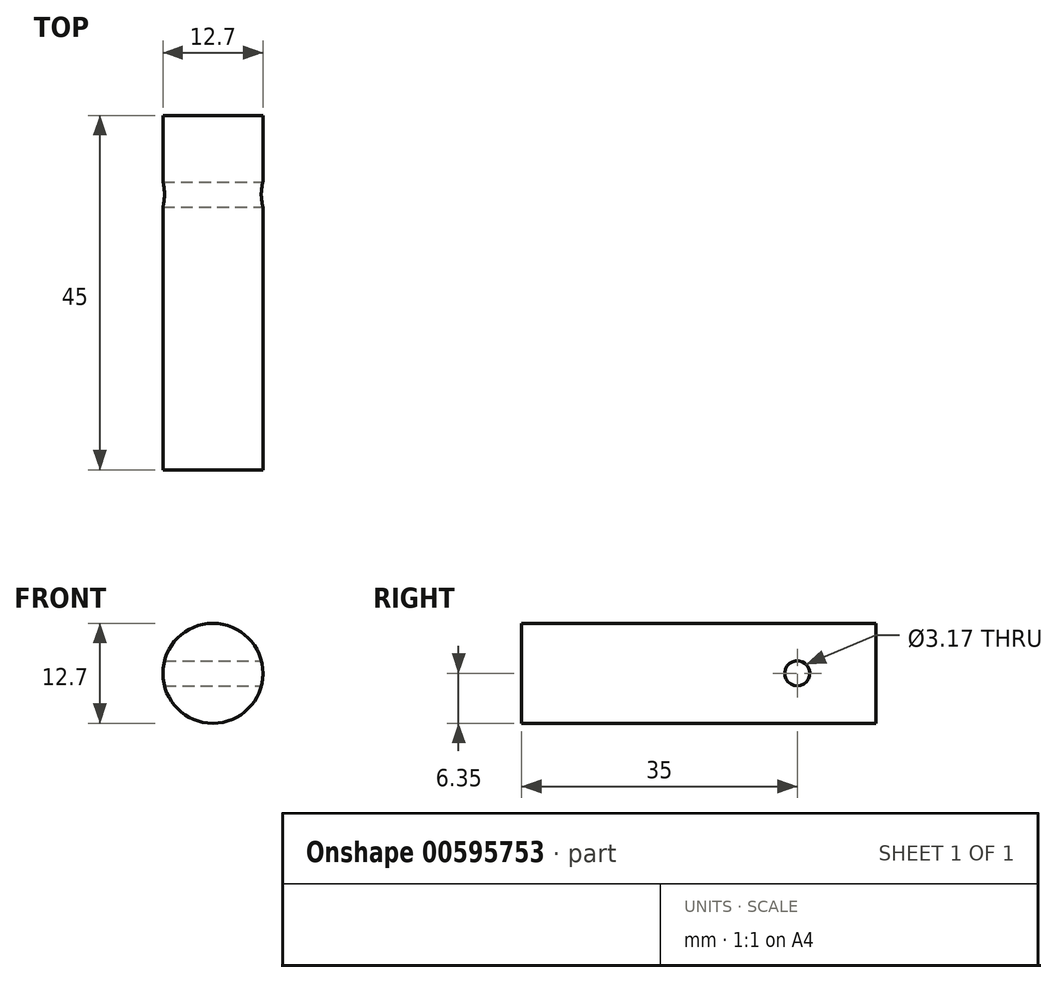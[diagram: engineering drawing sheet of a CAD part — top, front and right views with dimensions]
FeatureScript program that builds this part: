
annotation { "Feature Type Name" : "Feature", "Feature Type Description" : "" }
export const myFeature = defineFeature(function(context is Context, id is Id, definition is map)
    precondition{}
    {
        {
            var Q0;
            Q0=qCreatedBy(makeId("Front.planeOp"),FACE);
            var sketch = newSketch(context, id + "F0", { "sketchPlane" : qUnion([Q0])});
            skCircle(sketch, "E0", {"center": v(0, 0) * mm, "radius": 6.35 * mm});
            skSolve(sketch);
        }
        {
            var Q0;
            Q0=makeQuery(id+"F0.imprint","IMPRINT",FACE,{"disambiguationData":[TD([[makeQuery(id+"F0.imprint","IMPRINT",EDGE,{"derivedFrom":sQuery(id+"F0.wireOp",EDGE,"E0")}),1.0]])]});
            extrude(context, id + "F1", {"entities" : qUnion([Q0]), "depth" : 45 * mm, "offsetDistance" : 25 * mm});
        }
        {
            var Q0;
            Q0=qCreatedBy(makeId("Right.planeOp"),FACE);
            var sketch = newSketch(context, id + "F2", { "sketchPlane" : qUnion([Q0])});
            skCircle(sketch, "E1", {"center": v(-10, 0) * mm, "radius": 1.59 * mm});
            skSolve(sketch);
        }
        {
            var Q0;
            Q0 = qSketchRegion(id + "F2", true);
            extrude(context, id + "F3", {"entities" : qUnion([Q0]), "operationType" : NewBodyOperationType.REMOVE, "oppositeDirection" : true, "depth" : 25 * mm, "offsetDistance" : 25 * mm, "symmetric" : true});
        }
    });
